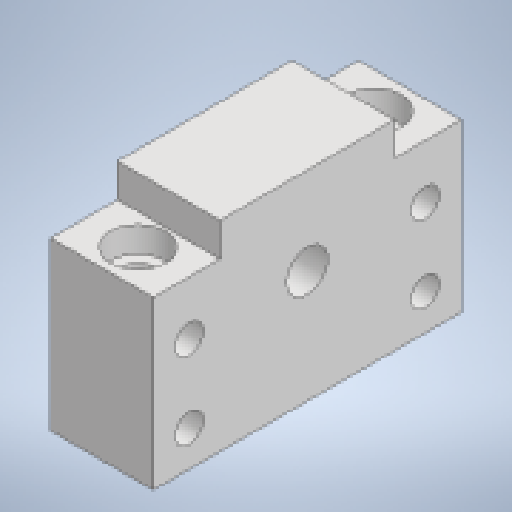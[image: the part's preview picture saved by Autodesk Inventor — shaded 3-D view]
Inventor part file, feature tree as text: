
AUTODESK INVENTOR PART (.ipt)
format: ipt  version: 2023 (Build 270158000, 158)  size: 194,048 bytes
history: native  units: mm
features: extrude x4, sketch x4
ambient origin geometry x8: Origin, YZ Plane, XZ Plane, XY Plane, X Axis, Y Axis, Z Axis, Center Point
bodies: Solid1 (feature_tree)
feature tree (8):
  extrude  "Extrusion1"  Depth=60.0mm
  extrude  "Extrusion2"  Depth=32.5mm
  extrude  "Extrusion3"  Depth=22.0mm
  extrude  "Extrusion4"  Depth=10.0mm
  sketch  "Sketch1"  dims[d0=34.0mm d1=60.0mm]
  sketch  "Sketch2"  dims[d2=39.0mm d3=32.5mm]
  sketch  "Sketch3"  dims[d4=5.5mm d6=22.0mm]
  sketch  "Sketch4"  dims[d7=15.0mm d8=46.0mm d9=8.0mm d10=20.0mm d11=0.0mm d12=10.8mm d13=10.8mm d14=46.0mm d15=7.0mm d16=10.0mm d17=5.0mm d18=0.0mm d19=6.6mm d20=5.0mm d21=0.0mm d22=22.0mm d23=10.0mm d24=0.0mm]
